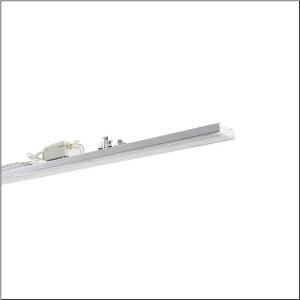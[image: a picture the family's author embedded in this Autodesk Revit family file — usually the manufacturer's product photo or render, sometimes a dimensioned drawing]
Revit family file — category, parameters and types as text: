
# Revit family: licross_21_recessed_ho_52te12dv4l2m3s4
name_source: partatom
category: Lighting Fixtures
units: mm (PartAtom-declared; Revit-internal decimal feet)

## family parameters
Cut with Voids When Loaded = No
Host = Face
Light Source = No
Part Type = Normal
Room Calculation Point = No
Round Connector Dimension = Use Diameter
Shared = No

## types (1)
- --- (1 x LED, 910 lm, 6.4 W, 4000K)
    Apparent Load = 6 VA
    CIE Flux Codes = 69 91 98 100 100
    Color Rendering = 80
    Color Temperature = 4000K
    Default Elevation = 1800 mm
    Description = Licross 21 Recessed HO, luminaire insert, of sheet steel, galvanised, coil coated, white, length: 2.250mm, width: 66mm, height: 67mm, LED rated luminous flux: 22.710lm, light colour: 840, SDCM (Standard Deviation of Colour Matching)MacAdam ≤ 3 SDCM (initial), control gear: DALI 2, with plug, 6-pole, with phase selection, for trunking rail, 9 or 11-core, mains connection: 220..240V, AC, 50/60Hz, rated input power: 129W, for trunking rail, 9-/11-core, internal wiring halogen-free, for emergency light function, converter,control gear: single battery element, battery: LiFePO4, 9Ah, primary optical cover: cover, of PMMA, light emission: direct distribution, primary light characteristic: symmetric, protection rating (complete): IP54, insulation class (complete): insulation class I (protective earthing), certification: CE, UKCA, protection symbol: D if used in an environment with non-conductive dust loads with corresponding accessories, impact resistance: IK06, permissible ambient temperature for indoor applications: +5..+30°C, standard: EN 60598-2-22, LABS conformity tested according to VDMA 24364:2018-05, reducing of maximum allowable ambient temperature of 5°C with ceiling mounting, corresponds to IFS (International Featured Standards) requirements for safety and quality in the food industry, The light source and the operating device comply with the requirements of the Ecodesign Regulation (EU) 2019/2020 and are replaceable in accordance with this regulation, packaging unit: 1 piece
    Height = 58 mm
    Lamp = 1 x LED
    Lamp Light Flux = 910 lm
    Lamp Power = 6.4 W
    Lamp count = 1
    Length = 2250 mm
    Luminous efficacy = 142 lm/W
    Manufacturer = Siteco
    ModVariant = No
    Model = 52TE12DV4L2M3S4
    Mounting Place = Ceiling
    Mounting Type = Pendant
    Number of Poles = 1
    OnlyDefault = Yes
    Power Factor = 1
    Product Name = Licross 21 Recessed HO
    Product group = luminaire insert | ceiling pendant
    ProductGroupID = 901
    Protection Class = Protection class I
    Protection Degree = IP 54
    RLX_Detail_Level = 1
    RLX_Emergency_Light_Flux = 0 lm
    RLX_Emergency_Type = 0
    RLX_Emergency_Type_DB = No
    RlxData = <blob elided: 30173 chars, md5=82841f0e>
    Socket = socket
    Standby Power = 0 W
    System Light Flux = 910 lm
    System Power = 6 W
    Type Comments = : emergency light operation: 3 h
    Type Image = l_1296930.jpg
    URL = http://relux.com
    VarID = @adj_110785
    Voltage = 0 V
    Weight = 0.00 kg
    Width = 66 mm

## geometry (parser evidence)
native form markers: Blend x4, Sweep x11
no freeform markers — native parametric forms only
